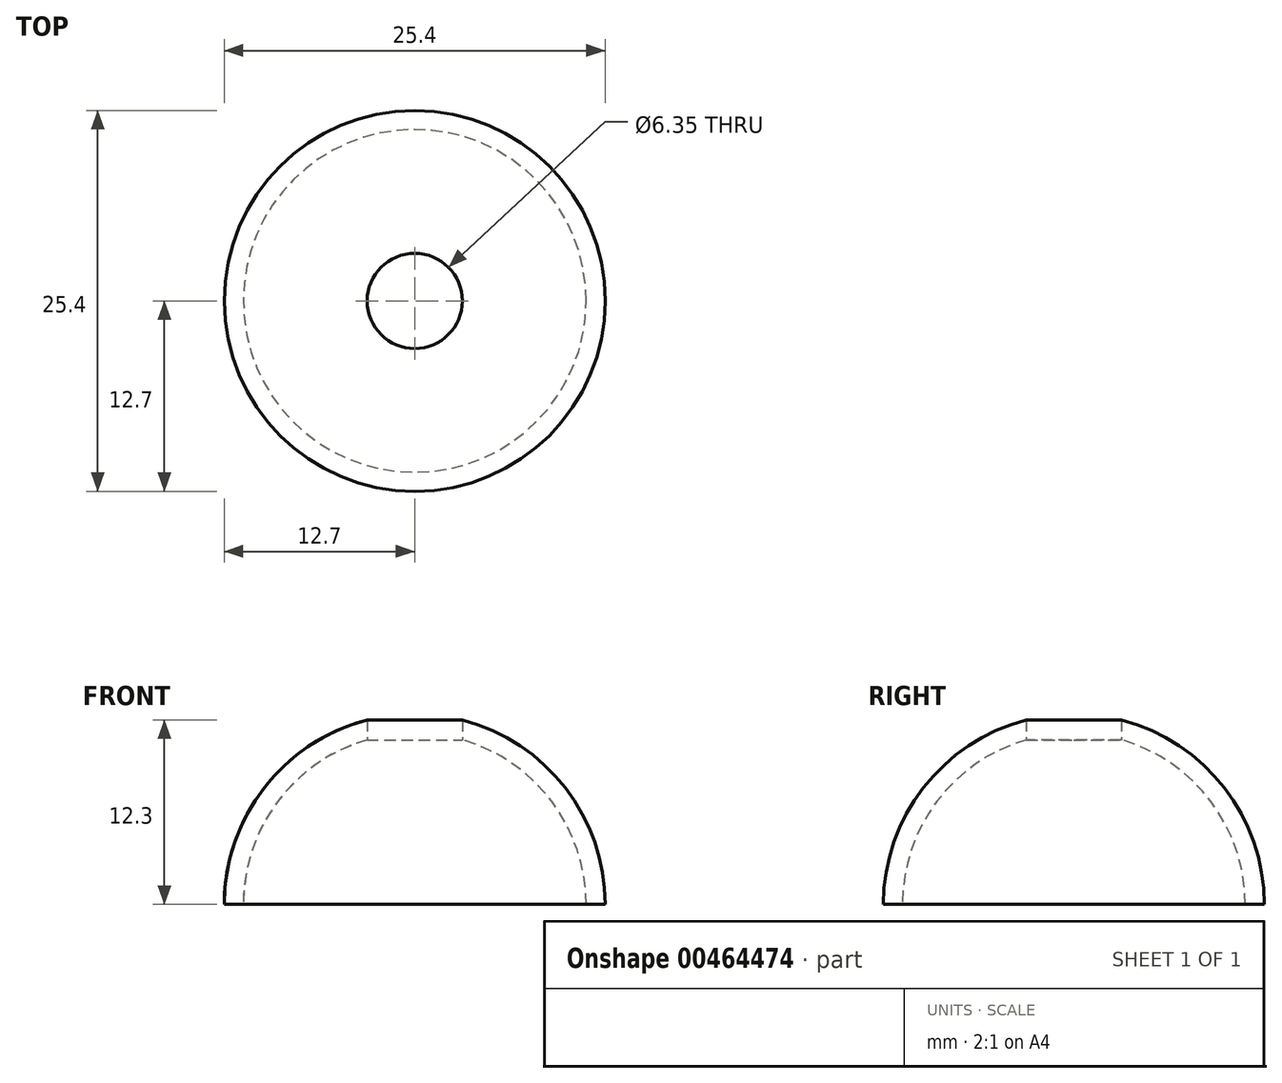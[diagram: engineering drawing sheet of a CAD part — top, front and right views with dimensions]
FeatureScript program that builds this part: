
annotation { "Feature Type Name" : "Feature", "Feature Type Description" : "" }
export const myFeature = defineFeature(function(context is Context, id is Id, definition is map)
    precondition{}
    {
        {
            var Q0;
            Q0=qCreatedBy(makeId("Front.planeOp"),FACE);
            var sketch = newSketch(context, id + "F0", { "sketchPlane" : qUnion([Q0])});
            skArc(sketch, "E0", {"start": v(-3.18, 12.3) * mm, "mid": v(-10.04, 7.78) * mm, "end": v(-12.7, 0) * mm});
            skArc(sketch, "E1", {"start": v(-3.17, 10.98) * mm, "mid": v(-9.14, 6.87) * mm, "end": v(-11.43, 0) * mm});
            skLineSegment(sketch, "E2", {"start": v(-3.18, 12.3) * mm, "end": v(-3.18, 10.98) * mm});
            skLineSegment(sketch, "E3", {"start": v(-11.43, 0) * mm, "end": v(-12.7, 0) * mm});
            skLineSegment(sketch, "E4", {"start": v(0, 0) * mm, "end": v(0, 6.8) * mm, "construction": true});
            skSolve(sketch);
        }
        {
            var Q0;
            Q0=makeQuery(id+"F0.imprint","IMPRINT",FACE,{"disambiguationData":[TD([[makeQuery(id+"F0.imprint","IMPRINT",EDGE,{"derivedFrom":sQuery(id+"F0.wireOp",EDGE,"E0")}),1.0]])]});
            var Q1;
            Q1=sQuery(id+"F0.wireOp",EDGE,"E4");
            revolve(context, id + "F1", {"entities" : qUnion([Q0]), "axis" : qUnion([Q1]), "revolveType" : RevolveType.FULL});
        }
    });
